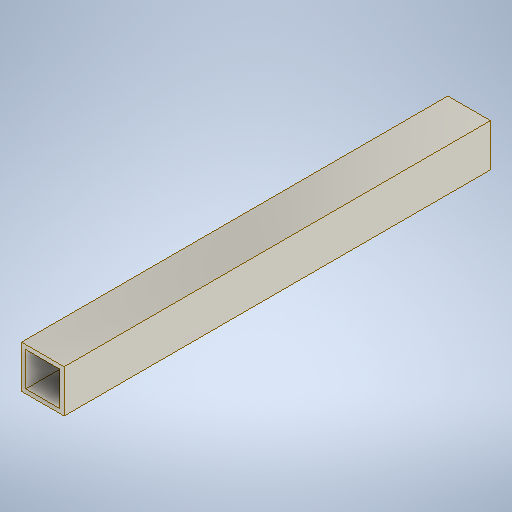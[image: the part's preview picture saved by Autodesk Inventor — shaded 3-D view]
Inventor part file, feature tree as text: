
AUTODESK INVENTOR PART (.ipt)
format: ipt  version: 2025.2 (Build 292293000, 293)  size: 245,760 bytes
history: native  units: mm
features: other x1, extrude x1, sketch x1
ambient origin geometry x8: Origin, YZ Plane, XZ Plane, XY Plane, X Axis, Y Axis, Z Axis, Center Point
bodies: Body1 (feature_tree)
feature tree (3):
  other  "Sólido1"
  extrude  "Extrusão1"  Depth=2.0mm
  sketch  "Esboço1"  dims[d0=20.0mm d1=2.0mm d2=200.0mm d3=0.0mm]
